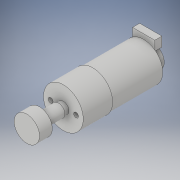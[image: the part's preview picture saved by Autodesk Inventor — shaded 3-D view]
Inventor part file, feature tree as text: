
AUTODESK INVENTOR PART (.ipt)
format: ipt  version: 2018.2 (Build 222227000, 227)  size: 154,112 bytes
history: native  units: in
note: dims shown in document units (in); Inventor stores cm internally (conversion verified against a paired STEP export)
features: sketch x9, extrude x8
ambient origin geometry x8: Origin, YZ Plane, XZ Plane, XY Plane, X Axis, Y Axis, Z Axis, Center Point
bodies: Solid1 (feature_tree)
feature tree (17):
  extrude  "Extrusion1"  Depth=1.2598in TaperAngle=0.0deg
  sketch  "Sketch2"  dims[d3=0.9843in d4=0.7283in d5=0.0in]
  sketch  "Sketch3"  dims[d6=0.2756in d7=0.1181in d8=0.0in]
  extrude  "Extrusion2"  Depth=0.7283in TaperAngle=0.0deg
  extrude  "Extrusion3"  Depth=0.1181in TaperAngle=0.0deg
  extrude  "Extrusion6"  Depth=0.2362in TaperAngle=0.0deg
  extrude  "Extrusion7"  Depth=0.5512in
  extrude  "Extrusion8"  Depth=0.1181in
  extrude  "Extrusion9"  Depth=0.1181in
  extrude  "Extrusion10"  Depth=0.1969in TaperAngle=0.0deg
  sketch  "Sketch1"  dims[d0=0.9449in d1=1.2598in d2=0.0in]
  sketch  "Sketch4"  dims[d15=0.5512in d16=0.2362in d17=0.0in]
  sketch  "Sketch7"  dims[d20=0.2756in d21=0.5512in]
  sketch  "Sketch8"  dims[d22=0.1772in d23=0.0in d24=0.1181in]
  sketch  "Sketch9"  dims[d25=0.315in d26=0.1181in]
  sketch  "Sketch10"  dims[d27=0.315in d28=0.1969in d29=0.0in]
  sketch  "Sketch11"  dims[d30=0.315in d31=0.4724in d32=0.0in d33=0.6299in d34=0.315in d35=0.0in]
